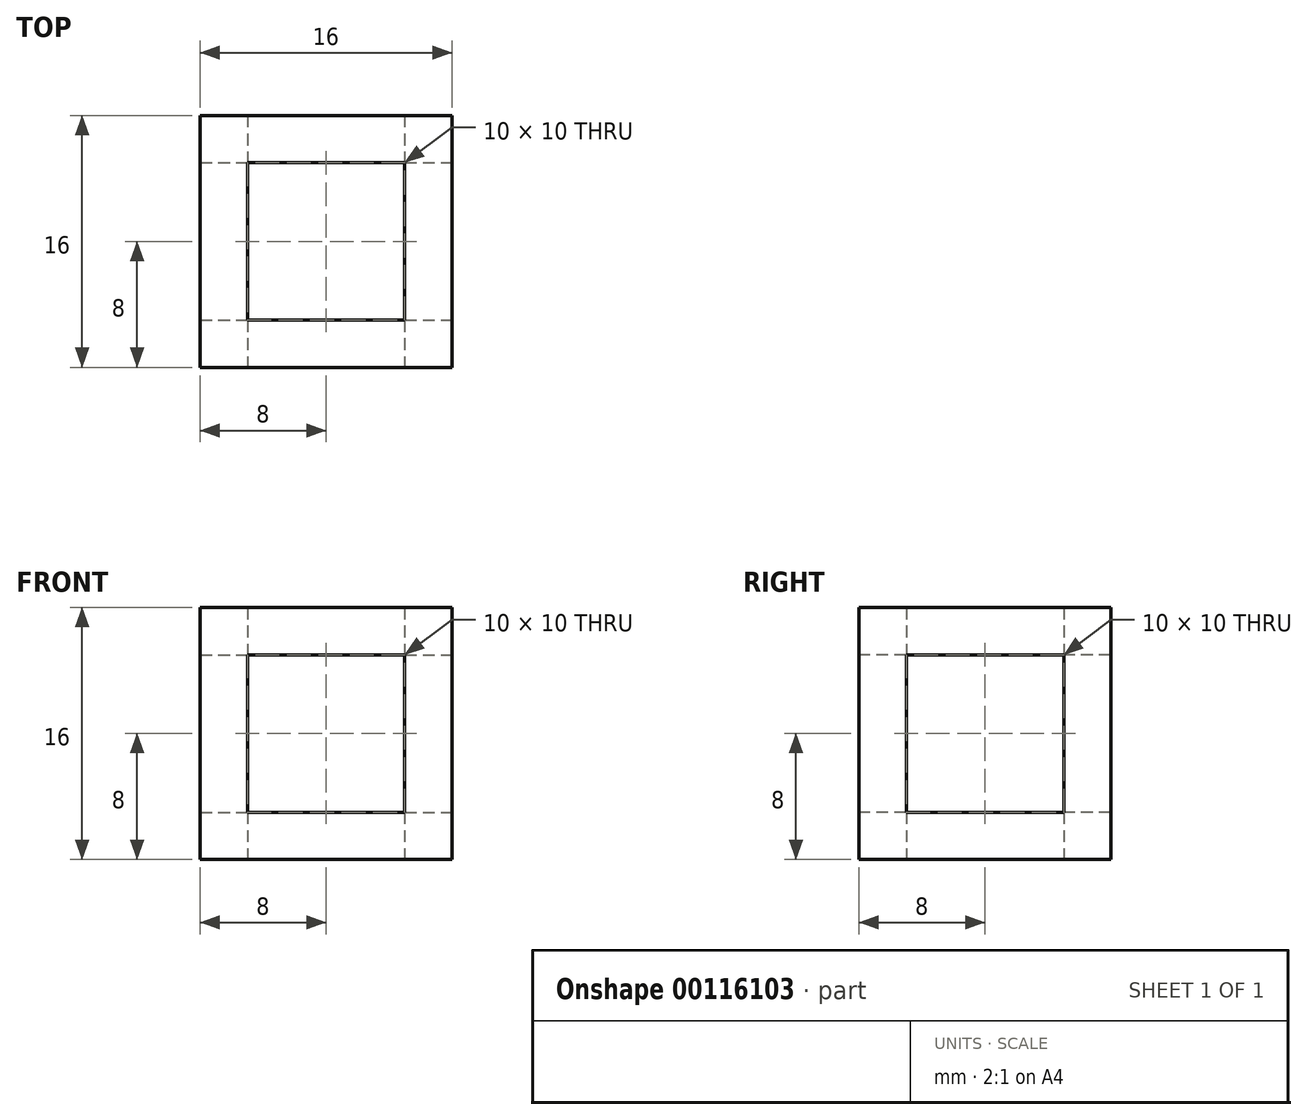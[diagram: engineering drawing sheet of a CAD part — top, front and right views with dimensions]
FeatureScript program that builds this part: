
annotation { "Feature Type Name" : "Feature", "Feature Type Description" : "" }
export const myFeature = defineFeature(function(context is Context, id is Id, definition is map)
    precondition{}
    {
        {
            var Q0;
            Q0=qCreatedBy(makeId("Top.planeOp"),FACE);
            var sketch = newSketch(context, id + "F0", { "sketchPlane" : qUnion([Q0])});
            skLineSegment(sketch, "E0.bottom", {"start": v(0, 0) * mm, "end": v(16, 0) * mm});
            skLineSegment(sketch, "E0.top", {"start": v(0, 16) * mm, "end": v(16, 16) * mm});
            skLineSegment(sketch, "E0.left", {"start": v(0, 0) * mm, "end": v(0, 16) * mm});
            skLineSegment(sketch, "E0.right", {"start": v(16, 0) * mm, "end": v(16, 16) * mm});
            skLineSegment(sketch, "E1.bottom", {"start": v(13, 13) * mm, "end": v(3, 13) * mm});
            skLineSegment(sketch, "E1.top", {"start": v(13, 3) * mm, "end": v(3, 3) * mm});
            skLineSegment(sketch, "E1.left", {"start": v(13, 13) * mm, "end": v(13, 3) * mm});
            skLineSegment(sketch, "E1.right", {"start": v(3, 13) * mm, "end": v(3, 3) * mm});
            skPoint(sketch, "E1.middle", {"position": v(8, 8) * mm});
            skPoint(sketch, "E1.middle.positionSnap0", {"position": v(0, 8) * mm});
            skPoint(sketch, "E1.middle.positionSnap1", {"position": v(8, 16) * mm});
            skPoint(sketch, "E1.centerSnap0", {"position": v(0, 8) * mm});
            skPoint(sketch, "E1.centerSnap1", {"position": v(8, 16) * mm});
            skSolve(sketch);
        }
        {
            var Q0;
            Q0=makeQuery(id+"F0.imprint","IMPRINT",FACE,{"disambiguationData":[TD([[makeQuery(id+"F0.imprint","IMPRINT",EDGE,{"derivedFrom":sQuery(id+"F0.wireOp",EDGE,"E0.bottom")}),1.0]])]});
            extrude(context, id + "F1", {"entities" : qUnion([Q0]), "depth" : 16 * mm});
        }
        {
            var Q0;
            Q0=makeQuery(id+"F1.opExtrude","SWEPT_FACE",FACE,{"disambiguationData":[OSD([sQuery(id+"F0.wireOp",EDGE,"E0.bottom")])]});
            var sketch = newSketch(context, id + "F2", { "sketchPlane" : qUnion([Q0])});
            skLineSegment(sketch, "E2.bottom", {"start": v(13, 13) * mm, "end": v(3, 13) * mm});
            skLineSegment(sketch, "E2.top", {"start": v(13, 3) * mm, "end": v(3, 3) * mm});
            skLineSegment(sketch, "E2.left", {"start": v(13, 13) * mm, "end": v(13, 3) * mm});
            skLineSegment(sketch, "E2.right", {"start": v(3, 13) * mm, "end": v(3, 3) * mm});
            skPoint(sketch, "E2.middle", {"position": v(8, 8) * mm});
            skPoint(sketch, "E2.middle.positionSnap0", {"position": v(16, 8) * mm});
            skPoint(sketch, "E2.middle.positionSnap1", {"position": v(8, 16) * mm});
            skPoint(sketch, "E2.centerSnap0", {"position": v(16, 8) * mm});
            skPoint(sketch, "E2.centerSnap1", {"position": v(8, 16) * mm});
            skSolve(sketch);
        }
        {
            var Q0;
            Q0 = qSketchRegion(id + "F2", true);
            extrude(context, id + "F3", {"entities" : qUnion([Q0]), "operationType" : NewBodyOperationType.REMOVE, "oppositeDirection" : true, "depth" : 25 * mm});
        }
        {
            var Q0;
            Q0=makeQuery(id+"F1.opExtrude","SWEPT_FACE",FACE,{"disambiguationData":[OSD([sQuery(id+"F0.wireOp",EDGE,"E0.right")])]});
            var sketch = newSketch(context, id + "F4", { "sketchPlane" : qUnion([Q0])});
            skLineSegment(sketch, "E3.bottom", {"start": v(13, 13) * mm, "end": v(3, 13) * mm});
            skLineSegment(sketch, "E3.top", {"start": v(13, 3) * mm, "end": v(3, 3) * mm});
            skLineSegment(sketch, "E3.left", {"start": v(13, 13) * mm, "end": v(13, 3) * mm});
            skLineSegment(sketch, "E3.right", {"start": v(3, 13) * mm, "end": v(3, 3) * mm});
            skPoint(sketch, "E3.middle", {"position": v(8, 8) * mm});
            skPoint(sketch, "E3.middle.positionSnap0", {"position": v(0, 8) * mm});
            skPoint(sketch, "E3.middle.positionSnap1", {"position": v(8, 16) * mm});
            skPoint(sketch, "E3.centerSnap0", {"position": v(0, 8) * mm});
            skPoint(sketch, "E3.centerSnap1", {"position": v(8, 16) * mm});
            skSolve(sketch);
        }
        {
            var Q0;
            Q0 = qSketchRegion(id + "F4", true);
            extrude(context, id + "F5", {"entities" : qUnion([Q0]), "operationType" : NewBodyOperationType.REMOVE, "oppositeDirection" : true, "depth" : 25 * mm});
        }
    });
